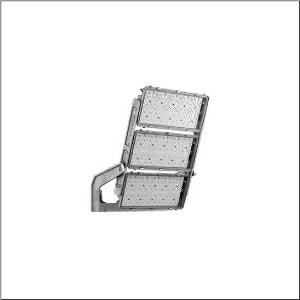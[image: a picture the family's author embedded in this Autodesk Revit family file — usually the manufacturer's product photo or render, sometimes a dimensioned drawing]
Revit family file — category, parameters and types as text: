
# Revit family: floodlight_fl_11_maxi_pro_remote___pl43_5xa779524a01aa_32ee
name_source: partatom
category: Lighting Fixtures
units: mm (PartAtom-declared; Revit-internal decimal feet)

## family parameters
Cut with Voids When Loaded = No
Host = Face
Light Source = No
Part Type = Normal
Room Calculation Point = No
Round Connector Dimension = Use Diameter
Shared = No

## types (1)
- --- (1 x LED, 130000 lm, 1334.7 W, 5700K)
    Apparent Load = 1335 VA
    CIE Flux Codes = 25 74 99 100 100
    Color Rendering = 90
    Color Temperature = 5700K
    Default Elevation = 1800 mm
    Description = Floodlight FL 11  maxi  pro Remote floodlight; light control with lens of PMMA; cover panel of toughened safety glass, transparent; light distribution: PL43, asymmetric direct distribution, LED; colour temperature: 5700K, rated luminous flux: 130.000lm, colour rendering: CRI > 90, light colour: 957; luminous efficacy: 97lm/W; brightness control: DMX+RDM; with terminal, 8-pole, max. 2.5mm², mains connection: 220..240V/380..400V AC, 50/60Hz, surge voltage resistance: line to ground: 10kV, ECG replaceable separately, no afterglow with DALI off / DMX off command, LED unit replaceable without ESD environment, dustproof LED module, dimming range 10..100%; 1335W floodlight with 3x LED unit of diecast aluminium, coated grey; length: 713mm / width: 651mm / height: 338mm; mounting bracket, of diecast aluminium, uncoated, natural, equipment: Power, protection rating (complete): IP66; insulation class (complete): insulation class I (protective earthing); certification: CE, ENEC, VDE; ball protection: ball impact resistance with accessories, impact resistance: IK07; only for outdoor installations, rated ambient temperature 10°C, permissible operating ambient temperature: -40..+30°C, permissible storage temperature: -40..+85°Cpackaging unit: 1 piece

Light Distribution: PL43
    Height = 320 mm
    Lamp = 1 x LED
    Lamp Light Flux = 130000 lm
    Lamp Power = 1334.7 W
    Lamp count = 1
    Length = 1002 mm
    Luminous efficacy = 97 lm/W
    Manufacturer = Siteco
    ModVariant = No
    Model = 5XA779524A01AA
    Mounting Place = Ceiling
    Mounting Type = Surface mounted
    Number of Poles = 1
    OnlyDefault = Yes
    Power Factor = 1
    Product Name = Floodlight FL 11 maxi pro Remote | PL43
    Product group = floodlight | ceiling mounted
    ProductGroupID = 302
    Protection Class = Protection class I
    Protection Degree = IP 66
    RLX_Detail_Level = 1
    RLX_Emergency_Light_Flux = 0 lm
    RLX_Emergency_Type = 0
    RLX_Emergency_Type_DB = No
    RlxData = <blob elided: 52429 chars, md5=cfa15c86>
    Socket = socket
    Standby Power = 0 W
    System Light Flux = 130000 lm
    System Power = 1335 W
    Type Comments = factory setting: luminous flux: 100 % | dim-lin: 255 | 920 mA
    Type Image = l_1349141.jpg
    URL = http://relux.com
    VarID = @adj_118151
    Voltage = 0 V
    Weight = 0.00 kg
    Width = 655 mm

## geometry (parser evidence)
native form markers: Blend x4, Sweep x14
no freeform markers — native parametric forms only
